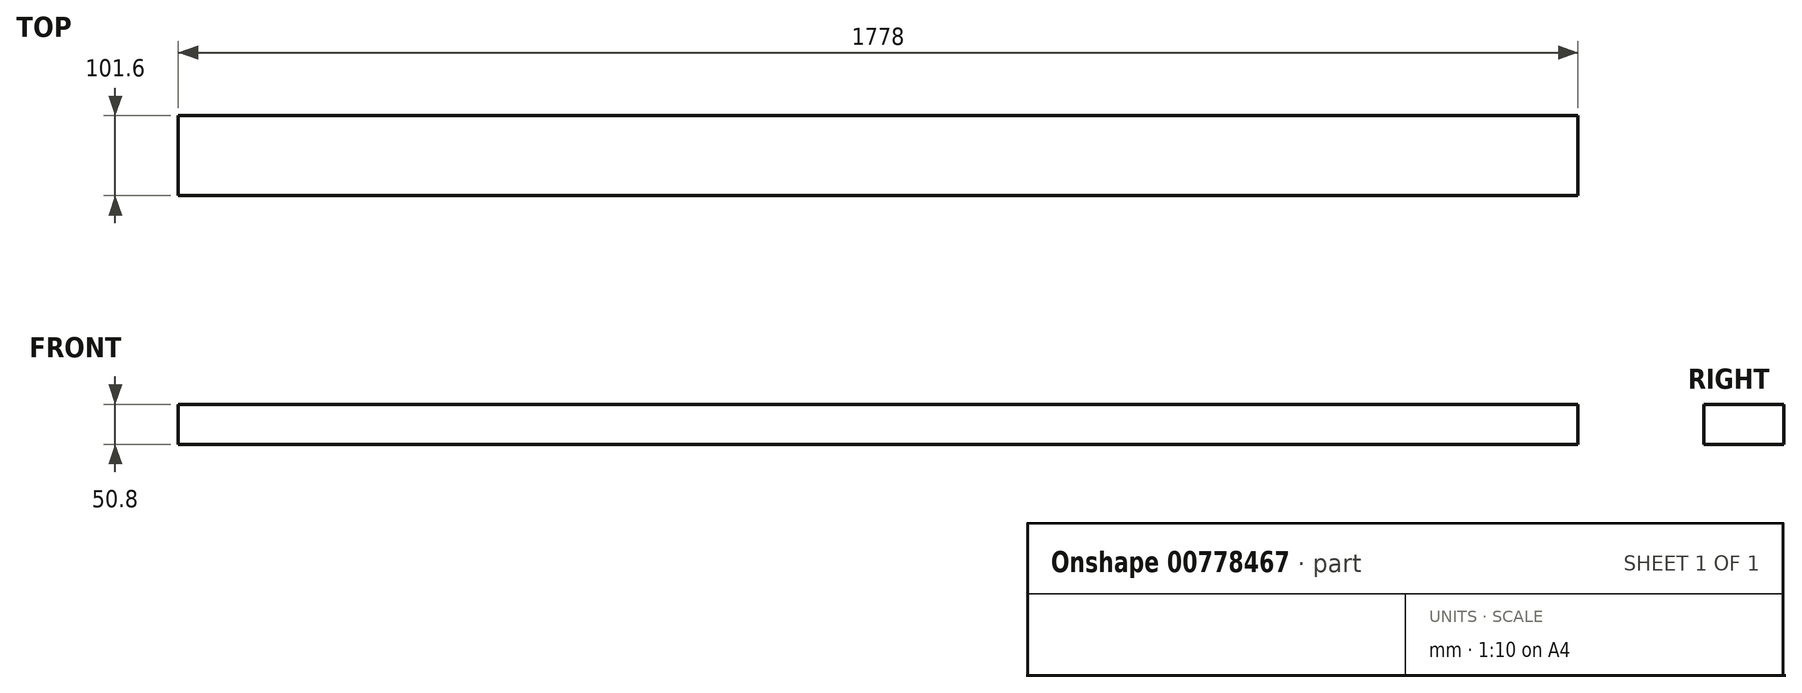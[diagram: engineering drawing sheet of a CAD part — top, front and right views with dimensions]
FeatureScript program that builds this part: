
annotation { "Feature Type Name" : "Feature", "Feature Type Description" : "" }
export const myFeature = defineFeature(function(context is Context, id is Id, definition is map)
    precondition{}
    {
        {
            var Q0;
            Q0=qCreatedBy(makeId("Top.planeOp"),FACE);
            var sketch = newSketch(context, id + "F0", { "sketchPlane" : qUnion([Q0])});
            skLineSegment(sketch, "E0.bottom", {"start": v(-889, -50.8) * mm, "end": v(889, -50.8) * mm});
            skLineSegment(sketch, "E0.top", {"start": v(-889, 50.8) * mm, "end": v(889, 50.8) * mm});
            skLineSegment(sketch, "E0.left", {"start": v(-889, -50.8) * mm, "end": v(-889, 50.8) * mm});
            skLineSegment(sketch, "E0.right", {"start": v(889, -50.8) * mm, "end": v(889, 50.8) * mm});
            skPoint(sketch, "E0.middle", {"position": v(0, 0) * mm});
            skSolve(sketch);
        }
        {
            var Q0;
            Q0=makeQuery(id+"F0.imprint","IMPRINT",FACE,{"disambiguationData":[TD([[makeQuery(id+"F0.imprint","IMPRINT",EDGE,{"derivedFrom":sQuery(id+"F0.wireOp",EDGE,"E0.bottom")}),1.0]])]});
            extrude(context, id + "F1", {"entities" : qUnion([Q0]), "depth" : 50.8 * mm, "offsetDistance" : 25.4 * mm});
        }
    });
